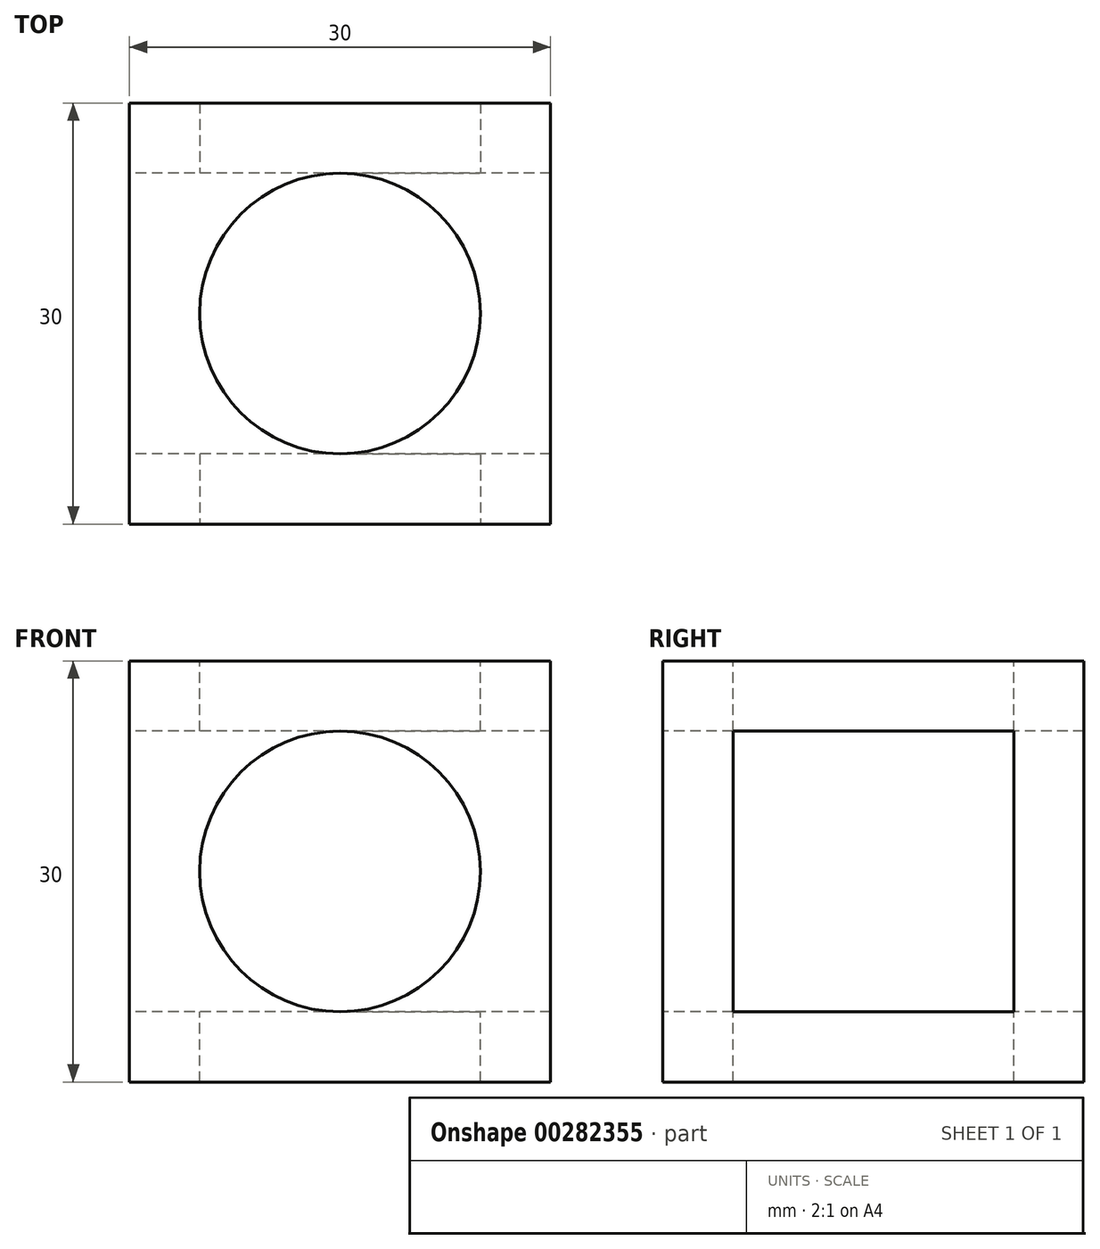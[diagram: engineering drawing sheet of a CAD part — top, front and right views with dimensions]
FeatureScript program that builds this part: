
annotation { "Feature Type Name" : "Feature", "Feature Type Description" : "" }
export const myFeature = defineFeature(function(context is Context, id is Id, definition is map)
    precondition{}
    {
        {
            var Q0;
            Q0=qCreatedBy(makeId("Right.planeOp"),FACE);
            var sketch = newSketch(context, id + "F0", { "sketchPlane" : qUnion([Q0])});
            skLineSegment(sketch, "E0.bottom", {"start": v(15, 15) * mm, "end": v(-15, 15) * mm});
            skLineSegment(sketch, "E0.top", {"start": v(15, -15) * mm, "end": v(-15, -15) * mm});
            skLineSegment(sketch, "E0.left", {"start": v(15, 15) * mm, "end": v(15, -15) * mm});
            skLineSegment(sketch, "E0.right", {"start": v(-15, 15) * mm, "end": v(-15, -15) * mm});
            skPoint(sketch, "E0.middle", {"position": v(0, 0) * mm});
            skLineSegment(sketch, "E1.0", {"start": v(-10, 10) * mm, "end": v(-10, -10) * mm});
            skLineSegment(sketch, "E1.1", {"start": v(10, 10) * mm, "end": v(-10, 10) * mm});
            skLineSegment(sketch, "E1.2", {"start": v(10, 10) * mm, "end": v(10, -10) * mm});
            skLineSegment(sketch, "E1.3", {"start": v(10, -10) * mm, "end": v(-10, -10) * mm});
            skSolve(sketch);
        }
        {
            var Q0;
            Q0=makeQuery(id+"F0.imprint","IMPRINT",FACE,{"disambiguationData":[TD([[makeQuery(id+"F0.imprint","IMPRINT",EDGE,{"derivedFrom":sQuery(id+"F0.wireOp",EDGE,"E0.bottom")}),1.0]])]});
            extrude(context, id + "F1", {"entities" : qUnion([Q0]), "depth" : 30 * mm});
        }
        {
            var Q0;
            Q0=makeQuery(id+"F1.opExtrude","SWEPT_FACE",FACE,{"disambiguationData":[OSD([sQuery(id+"F0.wireOp",EDGE,"E0.right")])]});
            var sketch = newSketch(context, id + "F2", { "sketchPlane" : qUnion([Q0])});
            skCircle(sketch, "E2", {"center": v(15, 0) * mm, "radius": 10 * mm});
            skPoint(sketch, "E2.centerSnap0", {"position": v(15, 15) * mm});
            skPoint(sketch, "E2.centerSnap1", {"position": v(0, 0) * mm});
            skSolve(sketch);
        }
        {
            var Q0;
            Q0=makeQuery(id+"F2.imprint","IMPRINT",FACE,{"disambiguationData":[TD([[makeQuery(id+"F2.imprint","IMPRINT",EDGE,{"derivedFrom":sQuery(id+"F2.wireOp",EDGE,"E2")}),1.0]])]});
            extrude(context, id + "F3", {"entities" : qUnion([Q0]), "operationType" : NewBodyOperationType.REMOVE, "endBound" : BoundingType.THROUGH_ALL, "oppositeDirection" : true, "depth" : 30 * mm});
        }
        {
            var Q0;
            Q0=makeQuery(id+"F1.opExtrude","SWEPT_FACE",FACE,{"disambiguationData":[OSD([sQuery(id+"F0.wireOp",EDGE,"E0.bottom")])]});
            var sketch = newSketch(context, id + "F4", { "sketchPlane" : qUnion([Q0])});
            skCircle(sketch, "E3", {"center": v(15, 0) * mm, "radius": 10 * mm});
            skPoint(sketch, "E3.centerSnap0", {"position": v(15, -15) * mm});
            skPoint(sketch, "E3.centerSnap1", {"position": v(0, 0) * mm});
            skSolve(sketch);
        }
        {
            var Q0;
            Q0 = qSketchRegion(id + "F4", true);
            extrude(context, id + "F5", {"entities" : qUnion([Q0]), "operationType" : NewBodyOperationType.REMOVE, "endBound" : BoundingType.THROUGH_ALL, "oppositeDirection" : true, "depth" : 30 * mm});
        }
    });
